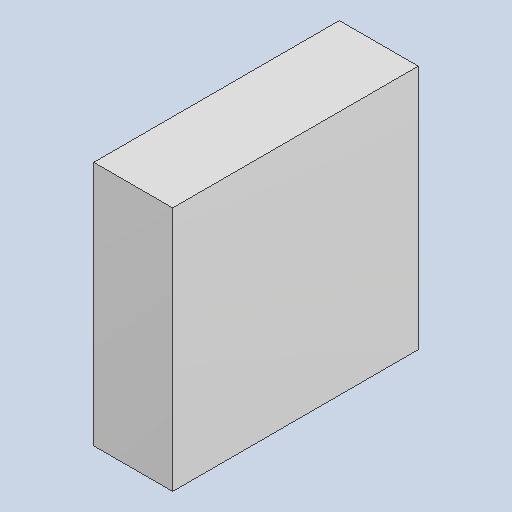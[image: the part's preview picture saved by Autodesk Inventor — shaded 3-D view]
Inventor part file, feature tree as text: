
AUTODESK INVENTOR PART (.ipt)
format: ipt  version: 2023.4 (Build 274418000, 418)  size: 81,408 bytes
history: native  units: mm
features: extrude x1
ambient origin geometry x8: Origin, YZ Plane, XZ Plane, XY Plane, X Axis, Y Axis, Z Axis, Center Point
bodies: Solid1 (feature_tree)
feature tree (1):
  extrude  "Extruded_1"  [1 undecoded]
note: 1 required parameter value undecoded (feature->parameter linkage not recoverable at this tier; creation-order binding heuristic only, values carry confidence <= 0.55)
